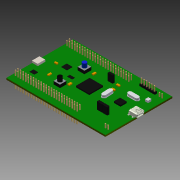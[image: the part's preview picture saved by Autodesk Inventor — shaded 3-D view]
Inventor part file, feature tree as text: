
AUTODESK INVENTOR PART (.ipt)
format: ipt  version: 2015 (Build 190159000, 159)  size: 2,894,848 bytes
history: native  units: in
note: dims shown in document units (in); Inventor stores cm internally (conversion verified against a paired STEP export)
features: projected_geometry x10, sketch x6, other x3, extrude x2, imported_body x2
ambient origin geometry x8: Origin, YZ Plane, XZ Plane, XY Plane, X Axis, Y Axis, Z Axis, Center Point
bodies: Body1 (feature_tree), Body2 (feature_tree)
feature tree (23):
  other  "_USB_Mini_B_SMD_buchse_-_Fase3_"
  other  "stm30f41"
  sketch  "Sketch1"  dims[d0=0.0992in d1=0.0309in]
  sketch  "Sketch2"  dims[d2=0.0312in d3=0.0309in]
  sketch  "Sketch3"  dims[d4=0.0984in]
  sketch  "Sketch4"  dims[d5=0.2756in]
  extrude  "Extrusion1"  Depth=0.0309in
  extrude  "Extrusion2"  Depth=0.0309in
  other  "LPattern17"
  imported_body  "Base1"
  imported_body  "Base2"
  projected_geometry  "Projected Loop1"
  projected_geometry  "Projected Loop2"
  projected_geometry  "Projected Loop3"
  projected_geometry  "Projected Loop4"
  projected_geometry  "Projected Loop5"
  projected_geometry  "Projected Loop6"
  projected_geometry  "Projected Loop7"
  projected_geometry  "Projected Loop8"
  sketch  "Sketch6"  dims[d6=0.0984in]
  projected_geometry  "Projected Loop9"
  sketch  "Sketch8"  dims[d7=0.1575in d8=2.4803in d9=0.0062in d10=0.0329in d11=0.4724in d12=0.0in d13=0.1181in d14=0.0in]
  projected_geometry  "Projected Loop10"
